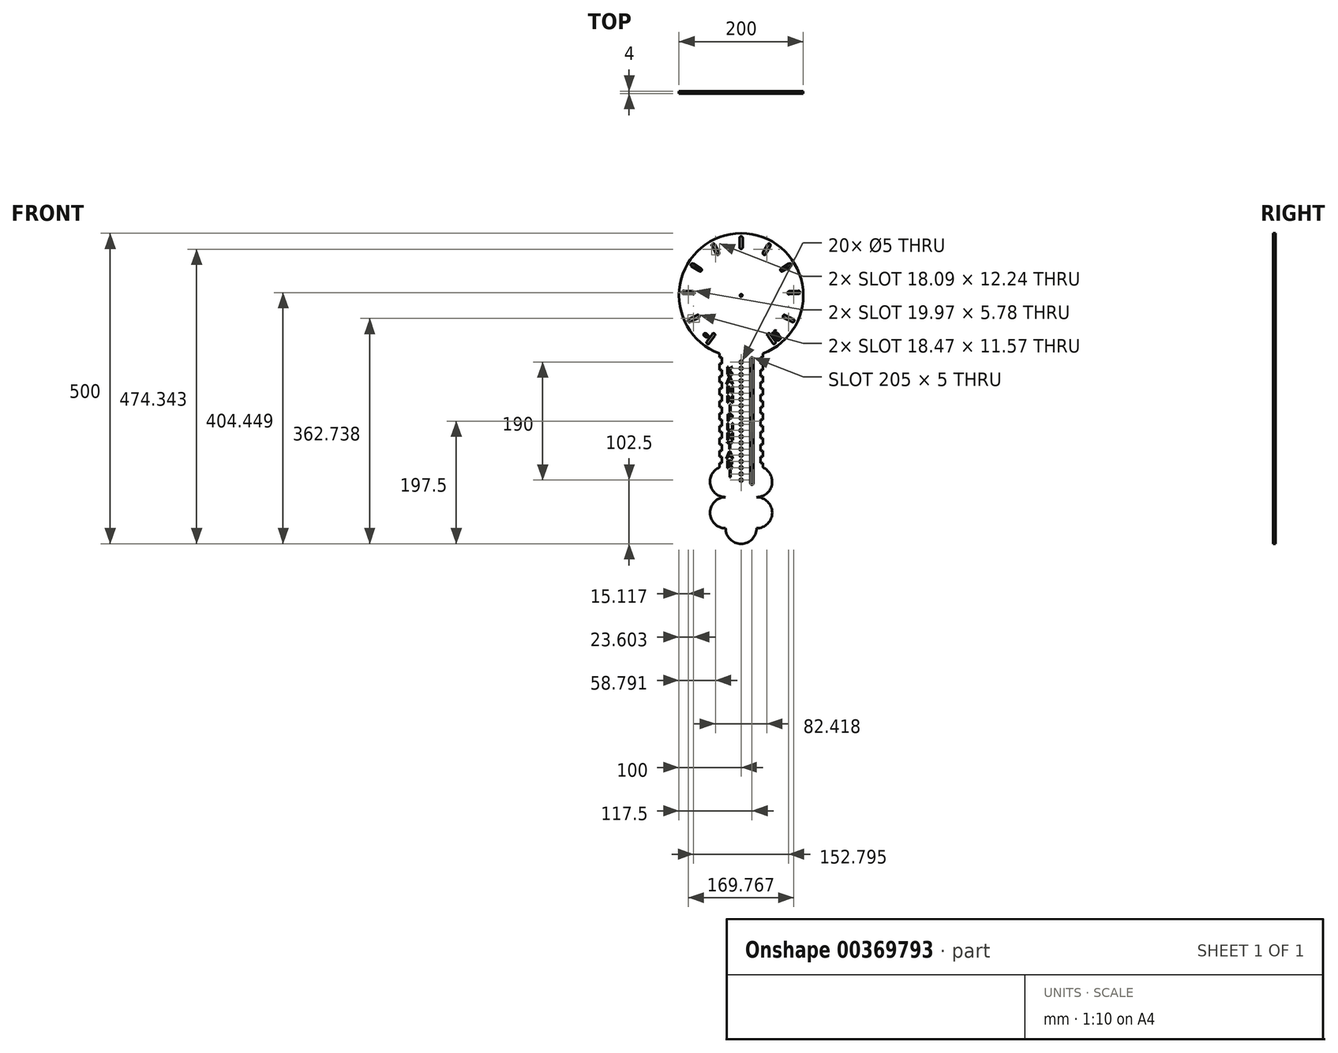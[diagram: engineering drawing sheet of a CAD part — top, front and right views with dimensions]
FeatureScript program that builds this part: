
annotation { "Feature Type Name" : "Feature", "Feature Type Description" : "" }
export const myFeature = defineFeature(function(context is Context, id is Id, definition is map)
    precondition{}
    {
        {
            var Q0;
            Q0=qCreatedBy(makeId("Front.planeOp"),FACE);
            var sketch = newSketch(context, id + "F0", { "sketchPlane" : qUnion([Q0])});
            skArc(sketch, "E0", {"start": v(35, -93.67) * mm, "mid": v(0, 100) * mm, "end": v(-35, -93.67) * mm});
            skLineSegment(sketch, "E1", {"start": v(0, 0) * mm, "end": v(0, -300) * mm, "construction": true});
            skLineSegment(sketch, "E2", {"start": v(-25, -96.82) * mm, "end": v(-25, -275) * mm, "construction": true});
            skArc(sketch, "E3", {"start": v(-25, -325) * mm, "mid": v(-50, -350) * mm, "end": v(-25, -375) * mm});
            skArc(sketch, "E4", {"start": v(-25, -375) * mm, "mid": v(0, -400) * mm, "end": v(25, -375) * mm});
            skArc(sketch, "E5", {"start": v(-35, -277.09) * mm, "mid": v(-49.47, -305.1) * mm, "end": v(-25, -325) * mm});
            skArc(sketch, "E6.MirrorCS", {"start": v(35, -277.09) * mm, "mid": v(49.47, -305.1) * mm, "end": v(25, -325) * mm});
            skArc(sketch, "E7.MirrorCS", {"start": v(25, -325) * mm, "mid": v(50, -350) * mm, "end": v(25, -375) * mm});
            skLineSegment(sketch, "E8", {"start": v(-25, -300) * mm, "end": v(25, -300) * mm, "construction": true});
            skLineSegment(sketch, "E9", {"start": v(-35, -93.67) * mm, "end": v(-35, -100) * mm});
            skLineSegment(sketch, "E10.MirrorCS", {"start": v(35, -93.67) * mm, "end": v(35, -100) * mm});
            skCircle(sketch, "E11", {"center": v(0, -107.5) * mm, "radius": 2.5 * mm});
            skCircle(sketch, "E12.0.1.0", {"center": v(0, -117.5) * mm, "radius": 2.5 * mm});
            skCircle(sketch, "E12.0.2.0", {"center": v(0, -127.5) * mm, "radius": 2.5 * mm});
            skCircle(sketch, "E12.0.3.0", {"center": v(0, -137.5) * mm, "radius": 2.5 * mm});
            skCircle(sketch, "E12.0.4.0", {"center": v(0, -147.5) * mm, "radius": 2.5 * mm});
            skCircle(sketch, "E12.0.5.0", {"center": v(0, -157.5) * mm, "radius": 2.5 * mm});
            skCircle(sketch, "E12.0.6.0", {"center": v(0, -167.5) * mm, "radius": 2.5 * mm});
            skCircle(sketch, "E12.0.7.0", {"center": v(0, -177.5) * mm, "radius": 2.5 * mm});
            skCircle(sketch, "E12.0.8.0", {"center": v(0, -187.5) * mm, "radius": 2.5 * mm});
            skCircle(sketch, "E12.0.9.0", {"center": v(0, -197.5) * mm, "radius": 2.5 * mm});
            skCircle(sketch, "E12.0.10.0", {"center": v(0, -207.5) * mm, "radius": 2.5 * mm});
            skCircle(sketch, "E12.0.11.0", {"center": v(0, -217.5) * mm, "radius": 2.5 * mm});
            skCircle(sketch, "E12.0.12.0", {"center": v(0, -227.5) * mm, "radius": 2.5 * mm});
            skCircle(sketch, "E12.0.13.0", {"center": v(0, -237.5) * mm, "radius": 2.5 * mm});
            skCircle(sketch, "E12.0.14.0", {"center": v(0, -247.5) * mm, "radius": 2.5 * mm});
            skCircle(sketch, "E12.0.15.0", {"center": v(0, -257.5) * mm, "radius": 2.5 * mm});
            skCircle(sketch, "E12.0.16.0", {"center": v(0, -267.5) * mm, "radius": 2.5 * mm});
            skCircle(sketch, "E12.0.17.0", {"center": v(0, -277.5) * mm, "radius": 2.5 * mm});
            skCircle(sketch, "E12.0.18.0", {"center": v(0, -287.5) * mm, "radius": 2.5 * mm});
            skCircle(sketch, "E12.0.19.0", {"center": v(0, -297.5) * mm, "radius": 2.5 * mm});
            skLineSegment(sketch, "E12.direction1", {"start": v(0, -107.5) * mm, "end": v(25, -107.5) * mm, "construction": true});
            skLineSegment(sketch, "E12.direction2", {"start": v(0, -107.5) * mm, "end": v(0, -117.5) * mm, "construction": true});
            skLineSegment(sketch, "E13.left", {"start": v(20, -102.5) * mm, "end": v(20, -302.5) * mm});
            skLineSegment(sketch, "E13.right", {"start": v(15, -102.5) * mm, "end": v(15, -302.5) * mm});
            skArc(sketch, "E14", {"start": v(15, -302.5) * mm, "mid": v(17.5, -305) * mm, "end": v(20, -302.5) * mm});
            skArc(sketch, "E15", {"start": v(20, -102.5) * mm, "mid": v(17.5, -100) * mm, "end": v(15, -102.5) * mm});
            skLineSegment(sketch, "E16", {"start": v(-35, -100) * mm, "end": v(35, -100) * mm, "construction": true});
            skLineSegment(sketch, "E17", {"start": v(0, 0) * mm, "end": v(0, 100) * mm, "construction": true});
            skArc(sketch, "E18", {"start": v(-2.5, 77.5) * mm, "mid": v(0, 75) * mm, "end": v(2.5, 77.5) * mm});
            skArc(sketch, "E19", {"start": v(2.5, 92.5) * mm, "mid": v(0, 95) * mm, "end": v(-2.5, 92.5) * mm});
            skLineSegment(sketch, "E20", {"start": v(2.5, 92.5) * mm, "end": v(2.5, 77.5) * mm});
            skLineSegment(sketch, "E21", {"start": v(-2.5, 92.5) * mm, "end": v(-2.5, 77.5) * mm});
            skLineSegment(sketch, "E22.1.0", {"start": v(42.66, 82.11) * mm, "end": v(35.39, 69) * mm});
            skArc(sketch, "E22.1.1", {"start": v(47.03, 79.7) * mm, "mid": v(46.06, 83.09) * mm, "end": v(42.66, 82.11) * mm});
            skArc(sketch, "E22.1.2", {"start": v(35.39, 69) * mm, "mid": v(36.36, 65.6) * mm, "end": v(39.76, 66.57) * mm});
            skLineSegment(sketch, "E22.1.3", {"start": v(47.03, 79.7) * mm, "end": v(39.76, 66.57) * mm});
            skLineSegment(sketch, "E22.2.0", {"start": v(77.12, 51.14) * mm, "end": v(64.4, 43.19) * mm});
            skArc(sketch, "E22.2.1", {"start": v(79.77, 46.9) * mm, "mid": v(80.56, 50.34) * mm, "end": v(77.12, 51.14) * mm});
            skArc(sketch, "E22.2.2", {"start": v(64.4, 43.19) * mm, "mid": v(63.6, 39.74) * mm, "end": v(67.05, 38.95) * mm});
            skLineSegment(sketch, "E22.2.3", {"start": v(79.77, 46.9) * mm, "end": v(67.05, 38.95) * mm});
            skLineSegment(sketch, "E22.3.0", {"start": v(92.24, 7.34) * mm, "end": v(77.26, 6.55) * mm});
            skArc(sketch, "E22.3.1", {"start": v(92.5, 2.34) * mm, "mid": v(94.87, 4.97) * mm, "end": v(92.24, 7.34) * mm});
            skArc(sketch, "E22.3.2", {"start": v(77.26, 6.55) * mm, "mid": v(74.9, 3.93) * mm, "end": v(77.52, 1.56) * mm});
            skLineSegment(sketch, "E22.3.3", {"start": v(92.5, 2.34) * mm, "end": v(77.52, 1.56) * mm});
            skLineSegment(sketch, "E22.4.0", {"start": v(84.23, -38.3) * mm, "end": v(70.75, -31.73) * mm});
            skArc(sketch, "E22.4.1", {"start": v(82.04, -42.8) * mm, "mid": v(85.39, -41.65) * mm, "end": v(84.23, -38.3) * mm});
            skArc(sketch, "E22.4.2", {"start": v(70.75, -31.73) * mm, "mid": v(67.4, -32.88) * mm, "end": v(68.56, -36.22) * mm});
            skLineSegment(sketch, "E22.4.3", {"start": v(82.04, -42.8) * mm, "end": v(68.56, -36.22) * mm});
            skLineSegment(sketch, "E22.5.0", {"start": v(55.1, -74.34) * mm, "end": v(46.5, -62.05) * mm});
            skArc(sketch, "E22.5.1", {"start": v(51, -77.2) * mm, "mid": v(54.49, -77.82) * mm, "end": v(55.1, -74.34) * mm});
            skArc(sketch, "E22.5.2", {"start": v(46.5, -62.05) * mm, "mid": v(43.02, -61.44) * mm, "end": v(42.4, -64.92) * mm});
            skLineSegment(sketch, "E22.5.3", {"start": v(51, -77.2) * mm, "end": v(42.4, -64.92) * mm});
            skLineSegment(sketch, "E22.anchor1", {"start": v(0, 0) * mm, "end": v(-2.5, 77.5) * mm, "construction": true});
            skLineSegment(sketch, "E22.anchor2", {"start": v(0, 0) * mm, "end": v(46.5, -62.05) * mm, "construction": true});
            skArc(sketch, "E23.MirrorCS", {"start": v(-51, -77.2) * mm, "mid": v(-54.49, -77.82) * mm, "end": v(-55.1, -74.34) * mm});
            skLineSegment(sketch, "E24.MirrorCS", {"start": v(-51, -77.2) * mm, "end": v(-42.4, -64.92) * mm});
            skArc(sketch, "E25.MirrorCS", {"start": v(-46.5, -62.05) * mm, "mid": v(-43.02, -61.44) * mm, "end": v(-42.4, -64.92) * mm});
            skLineSegment(sketch, "E26.MirrorCS", {"start": v(-55.1, -74.34) * mm, "end": v(-46.5, -62.05) * mm});
            skLineSegment(sketch, "E27.MirrorCS", {"start": v(-82.04, -42.8) * mm, "end": v(-68.56, -36.22) * mm});
            skArc(sketch, "E28.MirrorCS", {"start": v(-70.75, -31.73) * mm, "mid": v(-67.4, -32.88) * mm, "end": v(-68.56, -36.22) * mm});
            skLineSegment(sketch, "E29.MirrorCS", {"start": v(-84.23, -38.3) * mm, "end": v(-70.75, -31.73) * mm});
            skArc(sketch, "E30.MirrorCS", {"start": v(-82.04, -42.8) * mm, "mid": v(-85.39, -41.65) * mm, "end": v(-84.23, -38.3) * mm});
            skArc(sketch, "E31.MirrorCS", {"start": v(-77.26, 6.55) * mm, "mid": v(-74.9, 3.93) * mm, "end": v(-77.52, 1.56) * mm});
            skArc(sketch, "E32.MirrorCS", {"start": v(-92.5, 2.34) * mm, "mid": v(-94.87, 4.97) * mm, "end": v(-92.24, 7.34) * mm});
            skLineSegment(sketch, "E33.MirrorCS", {"start": v(-92.24, 7.34) * mm, "end": v(-77.26, 6.55) * mm});
            skLineSegment(sketch, "E34.MirrorCS", {"start": v(-92.5, 2.34) * mm, "end": v(-77.52, 1.56) * mm});
            skArc(sketch, "E35.MirrorCS", {"start": v(-79.77, 46.9) * mm, "mid": v(-80.56, 50.34) * mm, "end": v(-77.12, 51.14) * mm});
            skArc(sketch, "E36.MirrorCS", {"start": v(-64.4, 43.19) * mm, "mid": v(-63.6, 39.74) * mm, "end": v(-67.05, 38.95) * mm});
            skLineSegment(sketch, "E37.MirrorCS", {"start": v(-77.12, 51.14) * mm, "end": v(-64.4, 43.19) * mm});
            skLineSegment(sketch, "E38.MirrorCS", {"start": v(-79.77, 46.9) * mm, "end": v(-67.05, 38.95) * mm});
            skArc(sketch, "E39.MirrorCS", {"start": v(-47.03, 79.7) * mm, "mid": v(-46.06, 83.09) * mm, "end": v(-42.66, 82.11) * mm});
            skLineSegment(sketch, "E40.MirrorCS", {"start": v(-42.66, 82.11) * mm, "end": v(-35.39, 69) * mm});
            skLineSegment(sketch, "E41.MirrorCS", {"start": v(-47.03, 79.7) * mm, "end": v(-39.76, 66.57) * mm});
            skArc(sketch, "E42.MirrorCS", {"start": v(-35.39, 69) * mm, "mid": v(-36.36, 65.6) * mm, "end": v(-39.76, 66.57) * mm});
            skCircle(sketch, "E43", {"center": v(0, 0) * mm, "radius": 2 * mm});
            skLineSegment(sketch, "E44.bottom", {"start": v(-35, -100) * mm, "end": v(-31, -100) * mm});
            skLineSegment(sketch, "E44.top", {"start": v(-35, -110) * mm, "end": v(-31, -110) * mm});
            skLineSegment(sketch, "E44.right", {"start": v(-31, -100) * mm, "end": v(-31, -110) * mm});
            skLineSegment(sketch, "E45.0.1.0", {"start": v(-35, -130) * mm, "end": v(-31, -130) * mm});
            skLineSegment(sketch, "E45.0.1.1", {"start": v(-31, -120) * mm, "end": v(-31, -130) * mm});
            skLineSegment(sketch, "E45.0.1.2", {"start": v(-35, -120) * mm, "end": v(-31, -120) * mm});
            skLineSegment(sketch, "E45.0.2.0", {"start": v(-35, -150) * mm, "end": v(-31, -150) * mm});
            skLineSegment(sketch, "E45.0.2.1", {"start": v(-31, -140) * mm, "end": v(-31, -150) * mm});
            skLineSegment(sketch, "E45.0.2.2", {"start": v(-35, -140) * mm, "end": v(-31, -140) * mm});
            skLineSegment(sketch, "E45.0.3.0", {"start": v(-35, -170) * mm, "end": v(-31, -170) * mm});
            skLineSegment(sketch, "E45.0.3.1", {"start": v(-31, -160) * mm, "end": v(-31, -170) * mm});
            skLineSegment(sketch, "E45.0.3.2", {"start": v(-35, -160) * mm, "end": v(-31, -160) * mm});
            skLineSegment(sketch, "E45.0.4.0", {"start": v(-35, -190) * mm, "end": v(-31, -190) * mm});
            skLineSegment(sketch, "E45.0.4.1", {"start": v(-31, -180) * mm, "end": v(-31, -190) * mm});
            skLineSegment(sketch, "E45.0.4.2", {"start": v(-35, -180) * mm, "end": v(-31, -180) * mm});
            skLineSegment(sketch, "E45.0.5.0", {"start": v(-35, -210) * mm, "end": v(-31, -210) * mm});
            skLineSegment(sketch, "E45.0.5.1", {"start": v(-31, -200) * mm, "end": v(-31, -210) * mm});
            skLineSegment(sketch, "E45.0.5.2", {"start": v(-35, -200) * mm, "end": v(-31, -200) * mm});
            skLineSegment(sketch, "E45.0.6.0", {"start": v(-35, -230) * mm, "end": v(-31, -230) * mm});
            skLineSegment(sketch, "E45.0.6.1", {"start": v(-31, -220) * mm, "end": v(-31, -230) * mm});
            skLineSegment(sketch, "E45.0.6.2", {"start": v(-35, -220) * mm, "end": v(-31, -220) * mm});
            skLineSegment(sketch, "E45.0.7.0", {"start": v(-35, -250) * mm, "end": v(-31, -250) * mm});
            skLineSegment(sketch, "E45.0.7.1", {"start": v(-31, -240) * mm, "end": v(-31, -250) * mm});
            skLineSegment(sketch, "E45.0.7.2", {"start": v(-35, -240) * mm, "end": v(-31, -240) * mm});
            skLineSegment(sketch, "E45.0.8.0", {"start": v(-35, -270) * mm, "end": v(-31, -270) * mm});
            skLineSegment(sketch, "E45.0.8.1", {"start": v(-31, -260) * mm, "end": v(-31, -270) * mm});
            skLineSegment(sketch, "E45.0.8.2", {"start": v(-35, -260) * mm, "end": v(-31, -260) * mm});
            skLineSegment(sketch, "E45.direction1", {"start": v(-35, -110) * mm, "end": v(-10, -110) * mm, "construction": true});
            skLineSegment(sketch, "E45.direction2", {"start": v(-35, -110) * mm, "end": v(-35, -130) * mm, "construction": true});
            skLineSegment(sketch, "E46.trimOffspring", {"start": v(-35, -270) * mm, "end": v(-35, -277.09) * mm});
            skLineSegment(sketch, "E47.trimOffspring", {"start": v(-35, -250) * mm, "end": v(-35, -260) * mm});
            skLineSegment(sketch, "E48.trimOffspring", {"start": v(-35, -230) * mm, "end": v(-35, -240) * mm});
            skLineSegment(sketch, "E49.trimOffspring", {"start": v(-35, -210) * mm, "end": v(-35, -220) * mm});
            skLineSegment(sketch, "E50.trimOffspring", {"start": v(-35, -190) * mm, "end": v(-35, -200) * mm});
            skLineSegment(sketch, "E51.trimOffspring", {"start": v(-35, -170) * mm, "end": v(-35, -180) * mm});
            skLineSegment(sketch, "E52.trimOffspring", {"start": v(-35, -150) * mm, "end": v(-35, -160) * mm});
            skLineSegment(sketch, "E53", {"start": v(-35, -110) * mm, "end": v(-35, -120) * mm});
            skLineSegment(sketch, "E54", {"start": v(-35, -130) * mm, "end": v(-35, -140) * mm});
            skLineSegment(sketch, "E55.MirrorCS", {"start": v(35, -100) * mm, "end": v(31, -100) * mm});
            skLineSegment(sketch, "E56.MirrorCS", {"start": v(35, -110) * mm, "end": v(31, -110) * mm});
            skLineSegment(sketch, "E57.MirrorCS", {"start": v(31, -180) * mm, "end": v(31, -190) * mm});
            skLineSegment(sketch, "E58.MirrorCS", {"start": v(35, -220) * mm, "end": v(31, -220) * mm});
            skLineSegment(sketch, "E59.MirrorCS", {"start": v(35, -160) * mm, "end": v(31, -160) * mm});
            skLineSegment(sketch, "E60.MirrorCS", {"start": v(35, -140) * mm, "end": v(31, -140) * mm});
            skLineSegment(sketch, "E61.MirrorCS", {"start": v(35, -120) * mm, "end": v(31, -120) * mm});
            skLineSegment(sketch, "E62.MirrorCS", {"start": v(35, -170) * mm, "end": v(31, -170) * mm});
            skLineSegment(sketch, "E63.MirrorCS", {"start": v(35, -150) * mm, "end": v(31, -150) * mm});
            skLineSegment(sketch, "E64.MirrorCS", {"start": v(31, -260) * mm, "end": v(31, -270) * mm});
            skLineSegment(sketch, "E65.MirrorCS", {"start": v(31, -120) * mm, "end": v(31, -130) * mm});
            skLineSegment(sketch, "E66.MirrorCS", {"start": v(31, -200) * mm, "end": v(31, -210) * mm});
            skLineSegment(sketch, "E67.MirrorCS", {"start": v(31, -220) * mm, "end": v(31, -230) * mm});
            skLineSegment(sketch, "E68.MirrorCS", {"start": v(35, -230) * mm, "end": v(31, -230) * mm});
            skLineSegment(sketch, "E69.MirrorCS", {"start": v(35, -200) * mm, "end": v(31, -200) * mm});
            skLineSegment(sketch, "E70.MirrorCS", {"start": v(35, -270) * mm, "end": v(31, -270) * mm});
            skLineSegment(sketch, "E71.MirrorCS", {"start": v(35, -180) * mm, "end": v(31, -180) * mm});
            skLineSegment(sketch, "E72.MirrorCS", {"start": v(35, -210) * mm, "end": v(31, -210) * mm});
            skLineSegment(sketch, "E73.MirrorCS", {"start": v(31, -140) * mm, "end": v(31, -150) * mm});
            skLineSegment(sketch, "E74.MirrorCS", {"start": v(31, -240) * mm, "end": v(31, -250) * mm});
            skLineSegment(sketch, "E75.MirrorCS", {"start": v(35, -250) * mm, "end": v(31, -250) * mm});
            skLineSegment(sketch, "E76.MirrorCS", {"start": v(31, -100) * mm, "end": v(31, -110) * mm});
            skLineSegment(sketch, "E77.MirrorCS", {"start": v(31, -160) * mm, "end": v(31, -170) * mm});
            skLineSegment(sketch, "E78.MirrorCS", {"start": v(35, -240) * mm, "end": v(31, -240) * mm});
            skLineSegment(sketch, "E79.MirrorCS", {"start": v(35, -260) * mm, "end": v(31, -260) * mm});
            skLineSegment(sketch, "E80.MirrorCS", {"start": v(35, -130) * mm, "end": v(31, -130) * mm});
            skLineSegment(sketch, "E81.MirrorCS", {"start": v(35, -190) * mm, "end": v(31, -190) * mm});
            skLineSegment(sketch, "E82.trimOffspring", {"start": v(35, -270) * mm, "end": v(35, -277.09) * mm});
            skLineSegment(sketch, "E83.trimOffspring", {"start": v(35, -250) * mm, "end": v(35, -260) * mm});
            skLineSegment(sketch, "E84.trimOffspring", {"start": v(35, -230) * mm, "end": v(35, -240) * mm});
            skLineSegment(sketch, "E85.trimOffspring", {"start": v(35, -210) * mm, "end": v(35, -220) * mm});
            skLineSegment(sketch, "E86.trimOffspring", {"start": v(35, -190) * mm, "end": v(35, -200) * mm});
            skLineSegment(sketch, "E87.trimOffspring", {"start": v(35, -170) * mm, "end": v(35, -180) * mm});
            skLineSegment(sketch, "E88.trimOffspring", {"start": v(35, -150) * mm, "end": v(35, -160) * mm});
            skLineSegment(sketch, "E89.trimOffspring", {"start": v(35, -130) * mm, "end": v(35, -140) * mm});
            skLineSegment(sketch, "E90.trimOffspring", {"start": v(35, -110) * mm, "end": v(35, -120) * mm});
            skSolve(sketch);
        }
        {
            var Q0;
            Q0 = qSketchRegion(id + "F0", true);
            extrude(context, id + "F1", {"entities" : qUnion([Q0]), "depth" : 4 * mm});
        }
        {
            var Q0;
            Q0=qCreatedBy(makeId("Front.planeOp"),FACE);
            var sketch = newSketch(context, id + "F2", { "sketchPlane" : qUnion([Q0])});
            skText(sketch, "E91", { "text": "K", "fontName": "OpenSans-Regular.ttf"});
            skText(sketch, "E92", { "text": "Ä", "fontName": "OpenSans-Regular.ttf"});
            skText(sketch, "E93", { "text": "N", "fontName": "OpenSans-Regular.ttf"});
            skText(sketch, "E94", { "text": "N", "fontName": "OpenSans-Regular.ttf"});
            skText(sketch, "E95", { "text": "I", "fontName": "OpenSans-Regular.ttf"});
            skLineSegment(sketch, "E96", {"start": v(-18, -127) * mm, "end": v(-18, -175.82) * mm, "construction": true});
            skText(sketch, "E97", { "text": "P", "fontName": "OpenSans-Regular.ttf"});
            skText(sketch, "E98", { "text": "U", "fontName": "OpenSans-Regular.ttf"});
            skText(sketch, "E99", { "text": "N", "fontName": "OpenSans-Regular.ttf"});
            skText(sketch, "E100", { "text": "T", "fontName": "OpenSans-Regular.ttf"});
            skText(sketch, "E101", { "text": "A", "fontName": "OpenSans-Regular.ttf"});
            skText(sketch, "E102", { "text": "R", "fontName": "OpenSans-Regular.ttf"});
            skText(sketch, "E103", { "text": "I", "fontName": "OpenSans-Regular.ttf"});
            skText(sketch, "E104", { "text": "0", "fontName": "OpenSans-Regular.ttf"});
            skText(sketch, "E105", { "text": "100", "fontName": "OpenSans-Regular.ttf"});
            skLineSegment(sketch, "E106", {"start": v(53.26, -66.47) * mm, "end": v(50.8, -68.2) * mm, "construction": true});
            skLineSegment(sketch, "E107", {"start": v(-53.26, -66.47) * mm, "end": v(-50.8, -68.2) * mm});
            const initialGuessF2  = {"E91": [-0.02365, -0.127, 1, 0, 0.012], "E92": [-0.0238, -0.143, 1, 0, 0.012], "E93": [-0.024, -0.158, 1, 0, 0.012], "E94": [-0.024, -0.173, 1, 0, 0.012], "E95": [-0.02004, -0.188, 1, 0, 0.012], "E97": [-0.02313, -0.203, 1, 0, 0.012], "E98": [-0.02385, -0.218, 1, 0, 0.012], "E99": [-0.024, -0.233, 1, 0, 0.012], "E100": [-0.02307, -0.248, 1, 0, 0.012], "E101": [-0.0238, -0.263, 1, 0, 0.012], "E102": [-0.02354, -0.278, 1, 0, 0.012], "E103": [-0.02004, -0.293, 1, 0, 0.012], "E104": [-0.05513, -0.06914, 0.57358, 0.81915, 0.008], "E105": [0.04775, -0.0586, 0.57358, -0.81915, 0.008]};
            skSetInitialGuess(sketch, initialGuessF2);
            skSolve(sketch);
        }
        {
            var Q0;
            Q0 = qSketchRegion(id + "F2", true);
            extrude(context, id + "F3", {"entities" : qUnion([Q0]), "operationType" : NewBodyOperationType.REMOVE, "depth" : 4 * mm, "hasSecondDirection" : true, "secondDirectionOppositeDirection" : false, "secondDirectionDepth" : 3 * mm});
        }
    });
